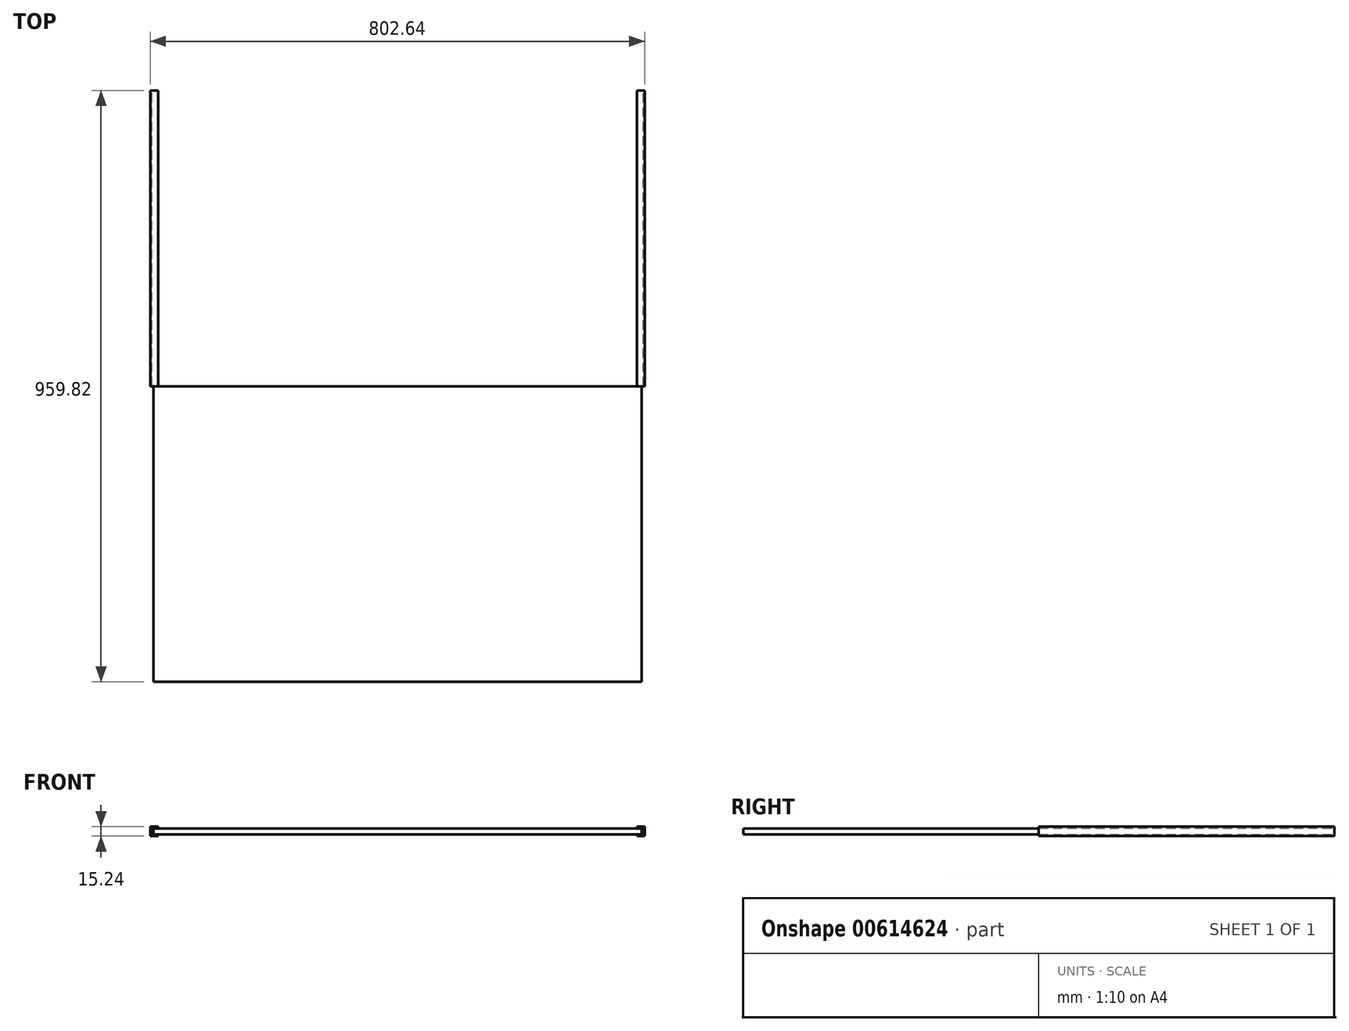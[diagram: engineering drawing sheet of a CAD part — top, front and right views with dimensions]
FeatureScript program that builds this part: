
annotation { "Feature Type Name" : "Feature", "Feature Type Description" : "" }
export const myFeature = defineFeature(function(context is Context, id is Id, definition is map)
    precondition{}
    {
        {
            var Q0;
            Q0=qCreatedBy(makeId("Front.planeOp"),FACE);
            var sketch = newSketch(context, id + "F0", { "sketchPlane" : qUnion([Q0])});
            skLineSegment(sketch, "E0", {"start": v(0, 0) * mm, "end": v(-12.7, 0) * mm});
            skLineSegment(sketch, "E1", {"start": v(-12.7, 0) * mm, "end": v(-12.7, -15.24) * mm});
            skLineSegment(sketch, "E2", {"start": v(-12.7, -15.24) * mm, "end": v(0, -15.24) * mm});
            skLineSegment(sketch, "E3", {"start": v(0, -15.24) * mm, "end": v(0, -12.7) * mm});
            skLineSegment(sketch, "E4", {"start": v(0, -12.7) * mm, "end": v(-10.16, -12.7) * mm});
            skLineSegment(sketch, "E5", {"start": v(-10.16, -12.7) * mm, "end": v(-10.16, -2.54) * mm});
            skLineSegment(sketch, "E6", {"start": v(-10.16, -2.54) * mm, "end": v(0, -2.54) * mm});
            skLineSegment(sketch, "E7", {"start": v(0, -2.54) * mm, "end": v(0, 0) * mm});
            skSolve(sketch);
        }
        {
            var Q0;
            Q0 = qSketchRegion(id + "F0", true);
            extrude(context, id + "F1", {"entities" : qUnion([Q0]), "depth" : 479.9 * mm, "offsetDistance" : 25.4 * mm});
        }
        {
            var Q0;
            Q0=makeQuery(id+"F1.opExtrude","CAP_FACE",FACE,{"disambiguationData":[OSD([sQuery(id+"F0.wireOp",EDGE,"E0"),sQuery(id+"F0.wireOp",EDGE,"E1"),sQuery(id+"F0.wireOp",EDGE,"E2"),sQuery(id+"F0.wireOp",EDGE,"E3"),sQuery(id+"F0.wireOp",EDGE,"E4"),sQuery(id+"F0.wireOp",EDGE,"E5"),sQuery(id+"F0.wireOp",EDGE,"E6"),sQuery(id+"F0.wireOp",EDGE,"E7")])],"isStart":false});
            var sketch = newSketch(context, id + "F2", { "sketchPlane" : qUnion([Q0])});
            skLineSegment(sketch, "E8.bottom", {"start": v(-7.62, -2.7) * mm, "end": v(388.62, -2.7) * mm});
            skLineSegment(sketch, "E8.top", {"start": v(-7.62, -12.7) * mm, "end": v(388.62, -12.7) * mm});
            skLineSegment(sketch, "E8.left", {"start": v(-7.62, -2.7) * mm, "end": v(-7.62, -12.7) * mm});
            skLineSegment(sketch, "E8.right", {"start": v(388.62, -2.7) * mm, "end": v(388.62, -12.7) * mm});
            skSolve(sketch);
        }
        {
            var Q0;
            Q0=makeQuery(id+"F2.imprint","IMPRINT",FACE,{"disambiguationData":[TD([[makeQuery(id+"F2.imprint","IMPRINT",EDGE,{"derivedFrom":sQuery(id+"F2.wireOp",EDGE,"E8.bottom")}),-1.0]])]});
            extrude(context, id + "F3", {"entities" : qUnion([Q0]), "depth" : 479.9 * mm, "offsetDistance" : 25.4 * mm});
        }
        {
            var Q0;
            Q0=makeQuery(id+"F3.opExtrude","SWEPT_FACE",FACE,{"disambiguationData":[OSD([sQuery(id+"F2.wireOp",EDGE,"E8.right")])]});
            cPlane(context, id + "F4", {"entities" : qUnion([Q0]), "cplaneType" : CPlaneType.OFFSET, "offset" : 0 * mm, "width" : 152.4 * mm, "height" : 152.4 * mm});
        }
        {
            var Q0;
            Q0=makeQuery(id+"F3.opExtrude","SWEPT_BODY",BODY,{"disambiguationData":[OSD([sQuery(id+"F2.wireOp",EDGE,"E8.bottom"),sQuery(id+"F2.wireOp",EDGE,"E8.top"),sQuery(id+"F2.wireOp",EDGE,"E8.left"),sQuery(id+"F2.wireOp",EDGE,"E8.right")])]});
            var Q1;
            Q1=makeQuery(id+"F1.opExtrude","SWEPT_BODY",BODY,{"disambiguationData":[OSD([sQuery(id+"F0.wireOp",EDGE,"E0"),sQuery(id+"F0.wireOp",EDGE,"E1"),sQuery(id+"F0.wireOp",EDGE,"E2"),sQuery(id+"F0.wireOp",EDGE,"E3"),sQuery(id+"F0.wireOp",EDGE,"E4"),sQuery(id+"F0.wireOp",EDGE,"E5"),sQuery(id+"F0.wireOp",EDGE,"E6"),sQuery(id+"F0.wireOp",EDGE,"E7")])]});
            var Q2;
            Q2=qCreatedBy(id+"F4.planeOp",FACE);
            mirror(context, id + "F5", {"operationType" : NewBodyOperationType.ADD, "entities" : qUnion([Q0, Q1]), "mirrorPlane" : qUnion([Q2])});
        }
    });
